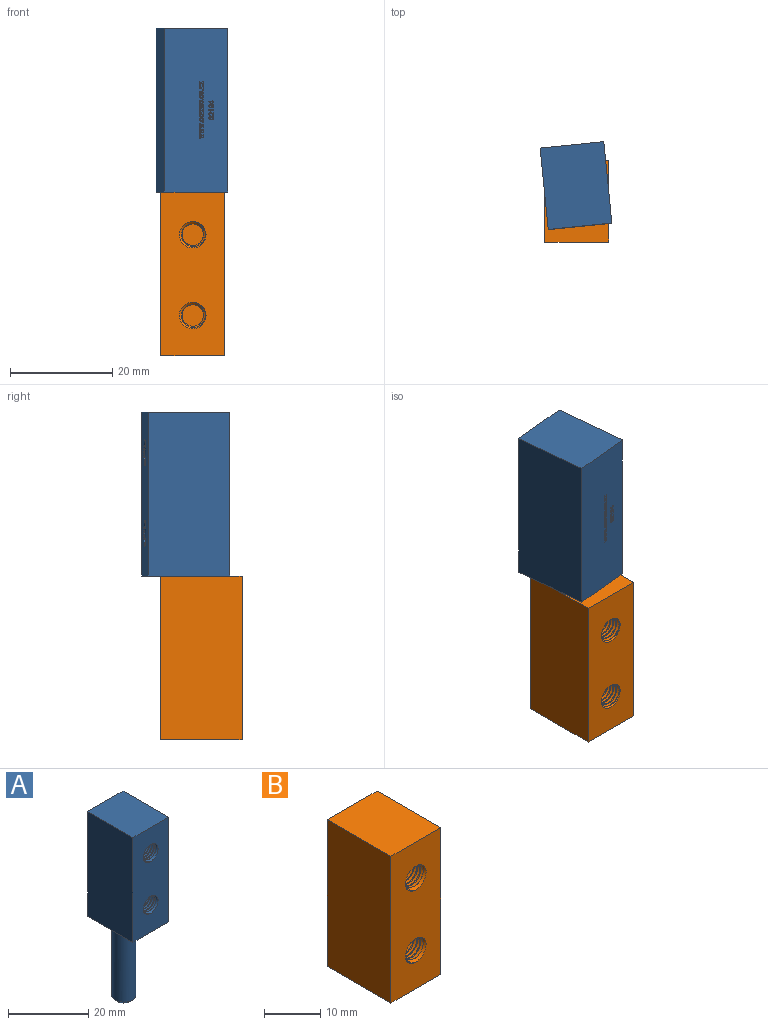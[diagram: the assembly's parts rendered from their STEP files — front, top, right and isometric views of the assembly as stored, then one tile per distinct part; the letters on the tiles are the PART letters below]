
ASSEMBLY  parts=2 mates=1
PART A: 293 faces, bbox 12.7x16.4x57.2 mm
  f0: cone r=2mm half-angle=45deg, axis (0,0,1), area 22.2mm2, adj f1,f17
  f1: cylinder r=3mm len=24mm, axis (0,0,1), area 452.4mm2, adj f0,f16
  f2: cone r=2.1mm half-angle=45deg, axis (0,-1,0), area 6.6mm2, adj f8,f13,f286,f288,f289
  f3: cylinder r=2.1mm len=4.2mm, axis (0,-1,0), area 12.2mm2, adj f4,f284,f287,f288,f289
  f4: cylinder r=2.1mm len=4.2mm, axis (0,-1,0), area 2.6mm2, adj f3,f5,f288,f289
  f5: cylinder r=2.1mm len=4.2mm, axis (0,-1,0), area 2.6mm2, adj f4,f6,f288,f289
  f6: cylinder r=2.1mm len=4.2mm, axis (0,-1,0), area 2.6mm2, adj f5,f7,f288,f289
  f7: cylinder r=2.1mm len=4.2mm, axis (0,-1,0), area 2.6mm2, adj f6,f8,f288,f289
  f8: cylinder r=2.1mm len=4.2mm, axis (0,-1,0), area 2.3mm2, adj f2,f7,f288,f289
  f9: cone r=2.1mm half-angle=45deg, axis (0,-1,0), area 6.6mm2, adj f10,f13,f290,f291,f292
  f10: cylinder r=2.1mm len=5.5mm, axis (0,-1,0), area 18.1mm2, adj f9,f285,f291,f292
  f11: plane 32x12.5mm, normal (0,1,0), area 394.7mm2, adj f12,f14,f15,f16,f18,f19,f20,f21
  f12: plane 32x16mm, normal (-1,0,0), area 512mm2, adj f11,f13,f15,f16
  f13: plane 32x12.5mm, normal (0,-1,0), area 357.5mm2, adj f2,f9,f12,f14,f15,f16
  f14: plane 32x16mm, normal (1,0,0), area 512mm2, adj f11,f13,f15,f16
  f15: plane 16x12.5mm, normal (0,0,1), area 200mm2, adj f11,f12,f13,f14
  f16: plane 16x12.5mm, normal (0,0,-1), area 171.7mm2, adj f1,f11,f12,f13,f14
  f17: plane 4x4mm, normal (0,0,-1), area 12.6mm2, adj f0
  f18: plane 0.25x0.13mm, normal (1,0,0), area 0mm2, adj f11,f19,f21,f22
  f19: plane 0.25x0.13mm, normal (0,0,1), area 0mm2, adj f11,f18,f20,f22
  f20: plane 0.25x0.13mm, normal (-1,0,0), area 0mm2, adj f11,f19,f21,f22
  f21: plane 0.25x0.13mm, normal (0,0,-1), area 0mm2, adj f11,f18,f20,f22
  f22: plane 0.13x0.13mm, normal (0,1,0), area 0mm2, adj f18,f19,f20,f21
  f23: extruded ~0.25x0.18mm, area 0.1mm2, adj f11,f24,f32,f33
  f24: plane 0.25x0.13mm, normal (-1,0,-0.1), area 0mm2, adj f11,f23,f25,f33
  f25: extruded ~0.3x0.27mm, area 0.1mm2, adj f11,f24,f26,f33
  f26: extruded ~0.38x0.33mm, area 0.1mm2, adj f11,f25,f27,f33
  f27: extruded ~0.38x0.33mm, area 0.1mm2, adj f11,f26,f28,f33
  f28: extruded ~0.29x0.25mm, area 0.1mm2, adj f11,f27,f29,f33
  f29: plane 0.25x0.13mm, normal (1,0,-0.1), area 0mm2, adj f11,f28,f30,f33
  f30: extruded ~0.25x0.16mm, area 0.1mm2, adj f11,f29,f31,f33
  f31: extruded ~0.26x0.25mm, area 0.1mm2, adj f11,f30,f32,f33
  f32: extruded ~0.26x0.25mm, area 0.1mm2, adj f11,f23,f31,f33
  f33: plane 0.76x0.63mm, normal (0,1,0), area 0.2mm2, adj f23,f24,f25,f26,f27,f28,f29,f30
  f34: extruded ~0.38x0.33mm, area 0.1mm2, adj f11,f35,f38,f39
  f35: extruded ~0.3x0.25mm, area 0.1mm2, adj f11,f34,f36,f39
  f36: cylinder r=0.33mm len=0.25mm, axis (0,-1,0), area 0.1mm2, adj f11,f35,f37,f39
  f37: extruded ~0.37x0.33mm, area 0.1mm2, adj f11,f36,f38,f39
  f38: extruded ~0.39x0.33mm, area 0.1mm2, adj f11,f34,f37,f39
  f39: plane 0.76x0.67mm, normal (0,1,0), area 0.2mm2, adj f34,f35,f36,f37,f38,f40,f41,f42
  f40: extruded ~0.26x0.25mm, area 0.1mm2, adj f39,f41,f43,f278
  f41: extruded ~0.26x0.25mm, area 0.1mm2, adj f39,f40,f42,f278
  f42: extruded ~0.27x0.25mm, area 0.1mm2, adj f39,f41,f43,f278
  f43: extruded ~0.26x0.25mm, area 0.1mm2, adj f39,f40,f42,f278
  f44: plane 0.25x0.13mm, normal (1,0,0), area 0mm2, adj f11,f45,f47,f48
  f45: plane 0.25x0.13mm, normal (0,0,1), area 0mm2, adj f11,f44,f46,f48
  f46: plane 0.25x0.13mm, normal (-1,0,0), area 0mm2, adj f11,f45,f47,f48
  f47: plane 0.25x0.13mm, normal (0,0,-1), area 0mm2, adj f11,f44,f46,f48
  f48: plane 0.13x0.13mm, normal (0,1,0), area 0mm2, adj f44,f45,f46,f47
  f49: plane 0.25x0.13mm, normal (1,0,0), area 0mm2, adj f11,f50,f61,f62
  f50: plane 0.73x0.25mm, normal (0,0,1), area 0.2mm2, adj f11,f49,f51,f62
  f51: plane 0.25x0.13mm, normal (-1,0,0), area 0mm2, adj f11,f50,f52,f62
  f52: plane 0.25x0.1mm, normal (0,0,-1), area 0mm2, adj f11,f51,f53,f62
  f53: extruded ~0.25x0.22mm, area 0.1mm2, adj f11,f52,f54,f62
  f54: extruded ~0.25x0.23mm, area 0.1mm2, adj f11,f53,f55,f62
  f55: extruded ~0.25x0.12mm, area 0mm2, adj f11,f54,f56,f62
  f56: plane 0.45x0.25mm, normal (0,0,-1), area 0.1mm2, adj f11,f55,f57,f62
  f57: plane 0.25x0.13mm, normal (1,0,0), area 0mm2, adj f11,f56,f58,f62
  f58: plane 0.44x0.25mm, normal (0,0,1), area 0.1mm2, adj f11,f57,f59,f62
  f59: extruded ~0.25x0.19mm, area 0.1mm2, adj f11,f58,f60,f62
  f60: extruded ~0.25x0.24mm, area 0.1mm2, adj f11,f59,f61,f62
  f61: plane 0.39x0.25mm, normal (0,0,-1), area 0.1mm2, adj f11,f49,f60,f62
  f62: plane 0.74x0.59mm, normal (0,1,0), area 0.2mm2, adj f49,f50,f51,f52,f53,f54,f55,f56
  f63: plane 0.63x0.25mm, normal (1,0,0), area 0.2mm2, adj f11,f64,f75,f76
  f64: plane 0.25x0.11mm, normal (0,0,1), area 0mm2, adj f11,f63,f65,f76
  f65: plane 0.52x0.44mm, normal (-0.64,0,0.77), area 0.2mm2, adj f11,f64,f66,f76
  f66: cylinder r=0.8mm len=0.25mm, axis (0,-1,0), area 0mm2, adj f11,f65,f67,f76
  f67: plane 0.27x0.25mm, normal (1,0,0), area 0.1mm2, adj f11,f66,f68,f76
  f68: plane 0.25x0.12mm, normal (0,0,1), area 0mm2, adj f11,f67,f69,f76
  f69: plane 0.58x0.25mm, normal (-1,0,0), area 0.1mm2, adj f11,f68,f70,f76
  f70: plane 0.25x0.09mm, normal (0,0,-1), area 0mm2, adj f11,f69,f71,f76
  f71: plane 0.48x0.4mm, normal (0.64,0,-0.77), area 0.2mm2, adj f11,f70,f72,f76
  f72: plane 0.25x0.07mm, normal (0.64,0,-0.76), area 0mm2, adj f11,f71,f73,f76
  f73: cylinder r=0.91mm len=0.25mm, axis (0,-1,0), area 0mm2, adj f11,f72,f74,f76
  f74: plane 0.32x0.25mm, normal (-1,0,0), area 0.1mm2, adj f11,f73,f75,f76
  f75: plane 0.25x0.12mm, normal (0,0,-1), area 0mm2, adj f11,f63,f74,f76
  f76: plane 0.73x0.63mm, normal (0,1,0), area 0.2mm2, adj f63,f64,f65,f66,f67,f68,f69,f70
  f77: extruded ~0.41x0.25mm, area 0.1mm2, adj f11,f78,f81,f82
  f78: extruded ~0.51x0.32mm, area 0.2mm2, adj f11,f77,f79,f82
  f79: extruded ~0.51x0.32mm, area 0.2mm2, adj f11,f78,f80,f82
  f80: extruded ~0.51x0.32mm, area 0.2mm2, adj f11,f79,f81,f82
  f81: extruded ~0.25x0.22mm, area 0.1mm2, adj f11,f77,f80,f82
  f82: plane 1.01x0.64mm, normal (0,1,0), area 0.3mm2, adj f77,f78,f79,f80,f81,f83,f84,f85
  f83: extruded ~0.32x0.25mm, area 0.1mm2, adj f82,f84,f87,f279
  f84: extruded ~0.25x0.13mm, area 0mm2, adj f82,f83,f85,f279
  f85: extruded ~0.39x0.25mm, area 0.1mm2, adj f82,f84,f86,f279
  f86: extruded ~0.39x0.25mm, area 0.1mm2, adj f82,f85,f87,f279
  f87: extruded ~0.39x0.25mm, area 0.1mm2, adj f82,f83,f86,f279
  f88: plane 0.49x0.25mm, normal (-1,0,0), area 0.1mm2, adj f11,f89,f100,f101
  f89: plane 0.25x0.13mm, normal (0,0,-1), area 0mm2, adj f11,f88,f90,f101
  f90: plane 0.65x0.25mm, normal (1,0,0), area 0.2mm2, adj f11,f89,f91,f101
  f91: cylinder r=0.24mm len=0.25mm, axis (0,-1,0), area 0mm2, adj f11,f90,f92,f101
  f92: extruded ~0.29x0.25mm, area 0.1mm2, adj f11,f91,f93,f101
  f93: extruded ~0.35x0.27mm, area 0.1mm2, adj f11,f92,f94,f101
  f94: extruded ~0.25x0.18mm, area 0.1mm2, adj f11,f93,f95,f101
  f95: extruded ~0.25x0.19mm, area 0.1mm2, adj f11,f94,f96,f101
  f96: plane 0.25x0.13mm, normal (1,0,0.1), area 0mm2, adj f11,f95,f97,f101
  f97: extruded ~0.32x0.28mm, area 0.1mm2, adj f11,f96,f98,f101
  f98: extruded ~0.31x0.28mm, area 0.1mm2, adj f11,f97,f99,f101
  f99: extruded ~0.41x0.28mm, area 0.1mm2, adj f11,f98,f100,f101
  f100: extruded ~0.25x0.2mm, area 0.1mm2, adj f11,f88,f99,f101
  f101: plane 1x0.65mm, normal (0,1,0), area 0.3mm2, adj f88,f89,f90,f91,f92,f93,f94,f95
  f102: extruded ~0.25x0.18mm, area 0.1mm2, adj f11,f103,f111,f112
  f103: plane 0.25x0.13mm, normal (-1,0,-0.1), area 0mm2, adj f11,f102,f104,f112
  f104: extruded ~0.3x0.27mm, area 0.1mm2, adj f11,f103,f105,f112
  f105: extruded ~0.38x0.33mm, area 0.1mm2, adj f11,f104,f106,f112
  f106: extruded ~0.38x0.33mm, area 0.1mm2, adj f11,f105,f107,f112
  f107: extruded ~0.29x0.25mm, area 0.1mm2, adj f11,f106,f108,f112
  f108: plane 0.25x0.13mm, normal (1,0,-0.1), area 0mm2, adj f11,f107,f109,f112
  f109: extruded ~0.25x0.16mm, area 0.1mm2, adj f11,f108,f110,f112
  f110: extruded ~0.26x0.25mm, area 0.1mm2, adj f11,f109,f111,f112
  f111: extruded ~0.26x0.25mm, area 0.1mm2, adj f11,f102,f110,f112
  f112: plane 0.76x0.63mm, normal (0,1,0), area 0.2mm2, adj f102,f103,f104,f105,f106,f107,f108,f109
  f113: extruded ~0.25x0.09mm, area 0mm2, adj f11,f114,f129,f130
  f114: extruded ~0.26x0.25mm, area 0.1mm2, adj f11,f113,f115,f130
  f115: extruded ~0.25x0.24mm, area 0.1mm2, adj f11,f114,f116,f130
  f116: extruded ~0.25x0.21mm, area 0.1mm2, adj f11,f115,f117,f130
  f117: extruded ~0.25x0.11mm, area 0mm2, adj f11,f116,f118,f130
  f118: extruded ~0.25x0.21mm, area 0.1mm2, adj f11,f117,f119,f130
  f119: plane 0.25x0.03mm, normal (-0.02,0,1), area 0mm2, adj f11,f118,f120,f130
  f120: extruded ~0.25x0.1mm, area 0mm2, adj f11,f119,f121,f130
  f121: extruded ~0.25x0.13mm, area 0mm2, adj f11,f120,f122,f130
  f122: extruded ~0.25x0.18mm, area 0.1mm2, adj f11,f121,f123,f130
  f123: plane 0.25x0.13mm, normal (1,0,0.1), area 0mm2, adj f11,f122,f124,f130
  f124: extruded ~0.33x0.25mm, area 0.1mm2, adj f11,f123,f125,f130
  f125: extruded ~0.28x0.25mm, area 0.1mm2, adj f11,f124,f126,f130
  f126: extruded ~0.25x0.11mm, area 0mm2, adj f11,f125,f127,f130
  f127: plane 0.25x0.16mm, normal (0,0,-1), area 0mm2, adj f11,f126,f128,f130
  f128: extruded ~0.32x0.25mm, area 0.1mm2, adj f11,f127,f129,f130
  f129: plane 0.25x0.13mm, normal (1,0,0), area 0mm2, adj f11,f113,f128,f130
  f130: plane 0.76x0.67mm, normal (0,1,0), area 0.3mm2, adj f113,f114,f115,f116,f117,f118,f119,f120
  f131: plane 0.25x0.04mm, normal (-0.02,0,1), area 0mm2, adj f130,f132,f136,f280
  f132: extruded ~0.25x0.1mm, area 0mm2, adj f130,f131,f133,f280
  f133: extruded ~0.25x0.2mm, area 0.1mm2, adj f130,f132,f134,f280
  f134: extruded ~0.25x0.14mm, area 0mm2, adj f130,f133,f135,f280
  f135: extruded ~0.25x0.17mm, area 0.1mm2, adj f130,f134,f136,f280
  f136: extruded ~0.25x0.19mm, area 0mm2, adj f130,f131,f135,f280
  f137: plane 0.25x0.13mm, normal (1,0,0), area 0mm2, adj f11,f138,f155,f156
  f138: plane 0.73x0.25mm, normal (0,0,1), area 0.2mm2, adj f11,f137,f139,f156
  f139: plane 0.25x0.13mm, normal (-1,0,0), area 0mm2, adj f11,f138,f140,f156
  f140: plane 0.25x0.11mm, normal (0,0,-1), area 0mm2, adj f11,f139,f141,f156
  f141: extruded ~0.25x0.21mm, area 0.1mm2, adj f11,f140,f142,f156
  f142: extruded ~0.25x0.19mm, area 0.1mm2, adj f11,f141,f143,f156
  f143: extruded ~0.25x0.22mm, area 0.1mm2, adj f11,f142,f144,f156
  f144: extruded ~0.25x0.24mm, area 0.1mm2, adj f11,f143,f145,f156
  f145: plane 0.5x0.25mm, normal (0,0,-1), area 0.1mm2, adj f11,f144,f146,f156
  f146: plane 0.25x0.13mm, normal (1,0,0), area 0mm2, adj f11,f145,f147,f156
  f147: plane 0.45x0.25mm, normal (0,0,1), area 0.1mm2, adj f11,f146,f148,f156
  f148: extruded ~0.25x0.18mm, area 0.1mm2, adj f11,f147,f149,f156
  f149: extruded ~0.25x0.21mm, area 0.1mm2, adj f11,f148,f150,f156
  f150: plane 0.42x0.25mm, normal (0,0,-1), area 0.1mm2, adj f11,f149,f151,f156
  f151: plane 0.25x0.13mm, normal (1,0,0), area 0mm2, adj f11,f150,f152,f156
  f152: plane 0.47x0.25mm, normal (0,0,1), area 0.1mm2, adj f11,f151,f153,f156
  f153: extruded ~0.25x0.16mm, area 0.1mm2, adj f11,f152,f154,f156
  f154: extruded ~0.26x0.25mm, area 0.1mm2, adj f11,f153,f155,f156
  f155: plane 0.37x0.25mm, normal (0,0,-1), area 0.1mm2, adj f11,f137,f154,f156
  f156: plane 0.97x0.74mm, normal (0,1,0), area 0.3mm2, adj f137,f138,f139,f140,f141,f142,f143,f144
  f157: extruded ~0.38x0.33mm, area 0.1mm2, adj f11,f158,f161,f162
  f158: extruded ~0.3x0.25mm, area 0.1mm2, adj f11,f157,f159,f162
  f159: cylinder r=0.33mm len=0.25mm, axis (0,-1,0), area 0.1mm2, adj f11,f158,f160,f162
  f160: extruded ~0.37x0.33mm, area 0.1mm2, adj f11,f159,f161,f162
  f161: extruded ~0.39x0.33mm, area 0.1mm2, adj f11,f157,f160,f162
  f162: plane 0.76x0.67mm, normal (0,1,0), area 0.2mm2, adj f157,f158,f159,f160,f161,f163,f164,f165
  f163: extruded ~0.26x0.25mm, area 0.1mm2, adj f162,f164,f166,f281
  f164: extruded ~0.26x0.25mm, area 0.1mm2, adj f162,f163,f165,f281
  f165: extruded ~0.27x0.25mm, area 0.1mm2, adj f162,f164,f166,f281
  f166: extruded ~0.26x0.25mm, area 0.1mm2, adj f162,f163,f165,f281
  f167: extruded ~0.25x0.18mm, area 0.1mm2, adj f11,f168,f176,f177
  f168: plane 0.25x0.13mm, normal (-1,0,-0.1), area 0mm2, adj f11,f167,f169,f177
  f169: extruded ~0.3x0.27mm, area 0.1mm2, adj f11,f168,f170,f177
  f170: extruded ~0.38x0.33mm, area 0.1mm2, adj f11,f169,f171,f177
  f171: extruded ~0.38x0.33mm, area 0.1mm2, adj f11,f170,f172,f177
  f172: extruded ~0.29x0.25mm, area 0.1mm2, adj f11,f171,f173,f177
  f173: plane 0.25x0.13mm, normal (1,0,-0.1), area 0mm2, adj f11,f172,f174,f177
  f174: extruded ~0.25x0.16mm, area 0.1mm2, adj f11,f173,f175,f177
  f175: extruded ~0.26x0.25mm, area 0.1mm2, adj f11,f174,f176,f177
  f176: extruded ~0.26x0.25mm, area 0.1mm2, adj f11,f167,f175,f177
  f177: plane 0.76x0.63mm, normal (0,1,0), area 0.2mm2, adj f167,f168,f169,f170,f171,f172,f173,f174
  f178: plane 0.25x0.13mm, normal (1,0,0), area 0mm2, adj f11,f179,f181,f182
  f179: plane 0.25x0.13mm, normal (0,0,1), area 0mm2, adj f11,f178,f180,f182
  f180: plane 0.25x0.13mm, normal (-1,0,0), area 0mm2, adj f11,f179,f181,f182
  f181: plane 0.25x0.13mm, normal (0,0,-1), area 0mm2, adj f11,f178,f180,f182
  f182: plane 0.13x0.13mm, normal (0,1,0), area 0mm2, adj f178,f179,f180,f181
  f183: plane 0.25x0.14mm, normal (1,0,0), area 0mm2, adj f11,f184,f200,f201
  f184: plane 0.73x0.25mm, normal (0.29,0,0.96), area 0.2mm2, adj f11,f183,f185,f201
  f185: plane 0.25x0.12mm, normal (-1,0,0), area 0mm2, adj f11,f184,f186,f201
  f186: plane 0.43x0.25mm, normal (-0.28,0,-0.96), area 0.1mm2, adj f11,f185,f187,f201
  f187: plane 0.25x0.15mm, normal (-0.23,0,-0.97), area 0mm2, adj f11,f186,f188,f201
  f188: plane 0.25x0.15mm, normal (-0.23,0,0.97), area 0mm2, adj f11,f187,f189,f201
  f189: plane 0.43x0.25mm, normal (-0.24,0,0.97), area 0.1mm2, adj f11,f188,f190,f201
  f190: plane 0.25x0.13mm, normal (-1,0,0), area 0mm2, adj f11,f189,f191,f201
  f191: plane 0.43x0.25mm, normal (-0.24,0,-0.97), area 0.1mm2, adj f11,f190,f192,f201
  f192: plane 0.25x0.13mm, normal (-0.22,0,-0.98), area 0mm2, adj f11,f191,f193,f201
  f193: plane 0.25x0.14mm, normal (-0.26,0,0.96), area 0mm2, adj f11,f192,f194,f201
  f194: plane 0.43x0.25mm, normal (-0.28,0,0.96), area 0.1mm2, adj f11,f193,f195,f201
  f195: plane 0.25x0.13mm, normal (-1,0,0), area 0mm2, adj f11,f194,f196,f201
  f196: plane 0.73x0.25mm, normal (0.28,0,-0.96), area 0.2mm2, adj f11,f195,f197,f201
  f197: plane 0.25x0.15mm, normal (1,0,0), area 0mm2, adj f11,f196,f198,f201
  f198: plane 0.43x0.25mm, normal (0.24,0,0.97), area 0.1mm2, adj f11,f197,f199,f201
  f199: plane 0.25x0.13mm, normal (0.22,0,0.98), area 0mm2, adj f11,f198,f200,f201
  f200: plane 0.56x0.25mm, normal (0.23,0,-0.97), area 0.1mm2, adj f11,f183,f199,f201
  f201: plane 0.99x0.73mm, normal (0,1,0), area 0.3mm2, adj f183,f184,f185,f186,f187,f188,f189,f190
  f202: plane 0.25x0.14mm, normal (1,0,0), area 0mm2, adj f11,f203,f219,f220
  f203: plane 0.73x0.25mm, normal (0.29,0,0.96), area 0.2mm2, adj f11,f202,f204,f220
  f204: plane 0.25x0.12mm, normal (-1,0,0), area 0mm2, adj f11,f203,f205,f220
  f205: plane 0.43x0.25mm, normal (-0.28,0,-0.96), area 0.1mm2, adj f11,f204,f206,f220
  f206: plane 0.25x0.15mm, normal (-0.23,0,-0.97), area 0mm2, adj f11,f205,f207,f220
  f207: plane 0.25x0.15mm, normal (-0.23,0,0.97), area 0mm2, adj f11,f206,f208,f220
  f208: plane 0.43x0.25mm, normal (-0.24,0,0.97), area 0.1mm2, adj f11,f207,f209,f220
  f209: plane 0.25x0.13mm, normal (-1,0,0), area 0mm2, adj f11,f208,f210,f220
  f210: plane 0.43x0.25mm, normal (-0.24,0,-0.97), area 0.1mm2, adj f11,f209,f211,f220
  f211: plane 0.25x0.13mm, normal (-0.22,0,-0.98), area 0mm2, adj f11,f210,f212,f220
  f212: plane 0.25x0.14mm, normal (-0.26,0,0.96), area 0mm2, adj f11,f211,f213,f220
  f213: plane 0.43x0.25mm, normal (-0.28,0,0.96), area 0.1mm2, adj f11,f212,f214,f220
  f214: plane 0.25x0.13mm, normal (-1,0,0), area 0mm2, adj f11,f213,f215,f220
  f215: plane 0.73x0.25mm, normal (0.28,0,-0.96), area 0.2mm2, adj f11,f214,f216,f220
  f216: plane 0.25x0.15mm, normal (1,0,0), area 0mm2, adj f11,f215,f217,f220
  f217: plane 0.43x0.25mm, normal (0.24,0,0.97), area 0.1mm2, adj f11,f216,f218,f220
  f218: plane 0.25x0.13mm, normal (0.22,0,0.98), area 0mm2, adj f11,f217,f219,f220
  f219: plane 0.56x0.25mm, normal (0.23,0,-0.97), area 0.1mm2, adj f11,f202,f218,f220
  f220: plane 0.99x0.73mm, normal (0,1,0), area 0.3mm2, adj f202,f203,f204,f205,f206,f207,f208,f209
  f221: plane 1x0.25mm, normal (0,0,-1), area 0.3mm2, adj f11,f222,f227,f228
  f222: plane 0.25x0.13mm, normal (1,0,0), area 0mm2, adj f11,f221,f223,f228
  f223: plane 0.78x0.25mm, normal (0,0,1), area 0.2mm2, adj f11,f222,f224,f228
  f224: extruded ~0.25x0.23mm, area 0.1mm2, adj f11,f223,f225,f228
  f225: plane 0.25x0.12mm, normal (0,0,1), area 0mm2, adj f11,f224,f226,f228
  f226: extruded ~0.28x0.25mm, area 0.1mm2, adj f11,f225,f227,f228
  f227: plane 0.25x0.08mm, normal (-1,0,0), area 0mm2, adj f11,f221,f226,f228
  f228: plane 1x0.36mm, normal (0,1,0), area 0.2mm2, adj f221,f222,f223,f224,f225,f226,f227
  f229: extruded ~0.28x0.26mm, area 0.1mm2, adj f11,f230,f238,f239
  f230: plane 0.25x0.13mm, normal (-1,0,0.1), area 0mm2, adj f11,f229,f231,f239
  f231: extruded ~0.25x0.15mm, area 0.1mm2, adj f11,f230,f232,f239
  f232: extruded ~0.35x0.25mm, area 0.1mm2, adj f11,f231,f233,f239
  f233: cylinder r=1.22mm len=0.25mm, axis (0,1,0), area 0mm2, adj f11,f232,f234,f239
  f234: extruded ~0.25x0.23mm, area 0.1mm2, adj f11,f233,f235,f239
  f235: extruded ~0.32x0.28mm, area 0.1mm2, adj f11,f234,f236,f239
  f236: extruded ~0.33x0.31mm, area 0.1mm2, adj f11,f235,f237,f239
  f237: extruded ~0.48x0.33mm, area 0.2mm2, adj f11,f236,f238,f239
  f238: extruded ~0.53x0.35mm, area 0.2mm2, adj f11,f229,f237,f239
  f239: plane 1.01x0.64mm, normal (0,1,0), area 0.3mm2, adj f229,f230,f231,f232,f233,f234,f235,f236
  f240: extruded ~0.25x0.21mm, area 0.1mm2, adj f239,f241,f243,f282
  f241: extruded ~0.25x0.2mm, area 0.1mm2, adj f239,f240,f242,f282
  f242: extruded ~0.25x0.22mm, area 0.1mm2, adj f239,f241,f243,f282
  f243: extruded ~0.25x0.21mm, area 0.1mm2, adj f239,f240,f242,f282
  f244: plane 0.25x0.13mm, normal (1,0,0), area 0mm2, adj f11,f245,f254,f255
  f245: plane 0.25x0.24mm, normal (0,0,1), area 0.1mm2, adj f11,f244,f246,f255
  f246: plane 0.44x0.25mm, normal (1,0,0), area 0.1mm2, adj f11,f245,f247,f255
  f247: plane 0.25x0.13mm, normal (0,0,1), area 0mm2, adj f11,f246,f248,f255
  f248: plane 0.62x0.47mm, normal (-0.61,0,0.79), area 0.2mm2, adj f11,f247,f249,f255
  f249: plane 0.25x0.09mm, normal (-1,0,0), area 0mm2, adj f11,f248,f250,f255
  f250: plane 0.62x0.25mm, normal (0,0,-1), area 0.2mm2, adj f11,f249,f251,f255
  f251: plane 0.25x0.13mm, normal (-1,0,0), area 0mm2, adj f11,f250,f252,f255
  f252: plane 0.25x0.13mm, normal (0,0,-1), area 0mm2, adj f11,f251,f253,f255
  f253: plane 0.25x0.13mm, normal (1,0,0), area 0mm2, adj f11,f252,f254,f255
  f254: plane 0.25x0.24mm, normal (0,0,-1), area 0.1mm2, adj f11,f244,f253,f255
  f255: plane 0.99x0.69mm, normal (0,1,0), area 0.3mm2, adj f244,f245,f246,f247,f248,f249,f250,f251
  f256: plane 0.28x0.25mm, normal (-1,0,0), area 0.1mm2, adj f255,f257,f258,f283
  f257: plane 0.36x0.28mm, normal (0.61,0,-0.79), area 0.1mm2, adj f255,f256,f258,f283
  f258: plane 0.36x0.25mm, normal (0,0,1), area 0.1mm2, adj f255,f256,f257,f283
  f259: plane 0.25x0.14mm, normal (1,0,0), area 0mm2, adj f11,f260,f276,f277
  f260: plane 0.73x0.25mm, normal (0.3,0,0.95), area 0.2mm2, adj f11,f259,f261,f277
  f261: plane 0.25x0.13mm, normal (-1,0,0), area 0mm2, adj f11,f260,f262,f277
  f262: plane 0.43x0.25mm, normal (-0.28,0,-0.96), area 0.1mm2, adj f11,f261,f263,f277
  f263: plane 0.25x0.15mm, normal (-0.23,0,-0.97), area 0mm2, adj f11,f262,f264,f277
  f264: plane 0.25x0.15mm, normal (-0.23,0,0.97), area 0mm2, adj f11,f263,f265,f277
  f265: plane 0.43x0.25mm, normal (-0.24,0,0.97), area 0.1mm2, adj f11,f264,f266,f277
  f266: plane 0.25x0.13mm, normal (-1,0,0), area 0mm2, adj f11,f265,f267,f277
  f267: plane 0.43x0.25mm, normal (-0.24,0,-0.97), area 0.1mm2, adj f11,f266,f268,f277
  f268: plane 0.25x0.13mm, normal (-0.22,0,-0.98), area 0mm2, adj f11,f267,f269,f277
  f269: plane 0.25x0.14mm, normal (-0.26,0,0.96), area 0mm2, adj f11,f268,f270,f277
  f270: plane 0.43x0.25mm, normal (-0.28,0,0.96), area 0.1mm2, adj f11,f269,f271,f277
  f271: plane 0.25x0.13mm, normal (-1,0,0), area 0mm2, adj f11,f270,f272,f277
  f272: plane 0.73x0.25mm, normal (0.28,0,-0.96), area 0.2mm2, adj f11,f271,f273,f277
  f273: plane 0.25x0.15mm, normal (1,0,0), area 0mm2, adj f11,f272,f274,f277
  f274: plane 0.43x0.25mm, normal (0.24,0,0.97), area 0.1mm2, adj f11,f273,f275,f277
  f275: plane 0.25x0.13mm, normal (0.22,0,0.98), area 0mm2, adj f11,f274,f276,f277
  f276: plane 0.56x0.25mm, normal (0.23,0,-0.97), area 0.1mm2, adj f11,f259,f275,f277
  f277: plane 1x0.73mm, normal (0,1,0), area 0.3mm2, adj f259,f260,f261,f262,f263,f264,f265,f266
  f278: plane 0.53x0.41mm, normal (0,1,0), area 0.2mm2, adj f40,f41,f42,f43
  f279: plane 0.78x0.38mm, normal (0,1,0), area 0.3mm2, adj f83,f84,f85,f86,f87
  f280: plane 0.36x0.24mm, normal (0,1,0), area 0.1mm2, adj f131,f132,f133,f134,f135,f136
  f281: plane 0.53x0.41mm, normal (0,1,0), area 0.2mm2, adj f163,f164,f165,f166
  f282: plane 0.42x0.38mm, normal (0,1,0), area 0.1mm2, adj f240,f241,f242,f243
  f283: plane 0.36x0.28mm, normal (0,1,0), area 0.1mm2, adj f256,f257,f258
  f284: plane 4.2x4.2mm, normal (0,-1,0), area 13.9mm2, adj f3
  f285: plane 4.86x4.81mm, normal (0,-1,0), area 16.6mm2, adj f10,f290,f291,f292
  f286: cylinder r=2.53mm len=5.28mm, axis (0,-1,0), area 12.8mm2, adj f2,f287,f288,f289
  f287: plane 0.6x0.31mm, normal (-0.71,0,0.71), area 0.2mm2, adj f3,f286,f288,f289
  f288: bspline ~5.55x5.07mm, area 47.3mm2, adj f2,f3,f4,f5,f6,f7,f8,f286
  f289: bspline ~5.45x5.07mm, area 44.1mm2, adj f2,f3,f4,f5,f6,f7,f8,f286
  f290: cylinder r=2.53mm len=5.93mm, axis (0,1,0), area 11.8mm2, adj f9,f285,f291,f292
  f291: bspline ~6.45x5.07mm, area 52.2mm2, adj f9,f10,f285,f290
  f292: bspline ~6.18x5.06mm, area 52.1mm2, adj f9,f10,f285,f290
PART B: 27 faces, bbox 12.7x16.4x32.2 mm
  f0: cone r=3mm half-angle=45deg, axis (0,0,-1), area 14.4mm2, adj f1,f16
  f1: cylinder r=3mm len=27.7mm, axis (0,0,-1), area 522.1mm2, adj f0,f26
  f2: cone r=2.1mm half-angle=45deg, axis (0,-1,0), area 6.6mm2, adj f8,f12,f19,f21,f22
  f3: cylinder r=2.1mm len=4.2mm, axis (0,-1,0), area 12.2mm2, adj f4,f17,f20,f21,f22
  f4: cylinder r=2.1mm len=4.2mm, axis (0,-1,0), area 2.6mm2, adj f3,f5,f21,f22
  f5: cylinder r=2.1mm len=4.2mm, axis (0,-1,0), area 2.6mm2, adj f4,f6,f21,f22
  f6: cylinder r=2.1mm len=4.2mm, axis (0,-1,0), area 2.6mm2, adj f5,f7,f21,f22
  f7: cylinder r=2.1mm len=4.2mm, axis (0,-1,0), area 2.6mm2, adj f6,f8,f21,f22
  f8: cylinder r=2.1mm len=4.2mm, axis (0,-1,0), area 2.3mm2, adj f2,f7,f21,f22
  f9: cone r=2.1mm half-angle=45deg, axis (0,-1,0), area 6.6mm2, adj f10,f12,f23,f24,f25
  f10: cylinder r=2.1mm len=5.5mm, axis (0,-1,0), area 18.1mm2, adj f9,f18,f24,f25
  f11: plane 32x16mm, normal (-1,0,0), area 512mm2, adj f12,f14,f15,f16
  f12: plane 32x12.5mm, normal (0,-1,0), area 357.5mm2, adj f2,f9,f11,f13,f15,f16
  f13: plane 32x16mm, normal (1,0,0), area 512mm2, adj f12,f14,f15,f16
  f14: plane 32x12.5mm, normal (0,1,0), area 400mm2, adj f11,f13,f15,f16
  f15: plane 16x12.5mm, normal (0,0,1), area 200mm2, adj f11,f12,f13,f14
  f16: plane 16x12.5mm, normal (0,0,-1), area 161.5mm2, adj f0,f11,f12,f13,f14
  f17: plane 4.2x4.2mm, normal (0,-1,0), area 13.9mm2, adj f3
  f18: plane 4.86x4.81mm, normal (0,-1,0), area 16.6mm2, adj f10,f23,f24,f25
  f19: cylinder r=2.53mm len=5.28mm, axis (0,-1,0), area 12.8mm2, adj f2,f20,f21,f22
  f20: plane 0.6x0.31mm, normal (-0.71,0,0.71), area 0.2mm2, adj f3,f19,f21,f22
  f21: bspline ~5.55x5.07mm, area 47.3mm2, adj f2,f3,f4,f5,f6,f7,f8,f19
  f22: bspline ~5.45x5.07mm, area 44.1mm2, adj f2,f3,f4,f5,f6,f7,f8,f19
  f23: cylinder r=2.53mm len=5.93mm, axis (0,1,0), area 11.8mm2, adj f9,f18,f24,f25
  f24: bspline ~6.45x5.07mm, area 52.2mm2, adj f9,f10,f18,f23
  f25: bspline ~6.18x5.06mm, area 52.1mm2, adj f9,f10,f18,f23
  f26: plane 6x6mm, normal (0,0,-1), area 28.3mm2, adj f1
PLACE A rot(axis=(0,0,-1),174.3deg) t=(-0.94,9.45,0)mm
PLACE B rot(axis=(0,-1,0),180deg) t=(0,-9.5,0)mm
MATE revolute A.f0 <-> B.f0  axis (0,0,-1) through (0,0,0)mm
